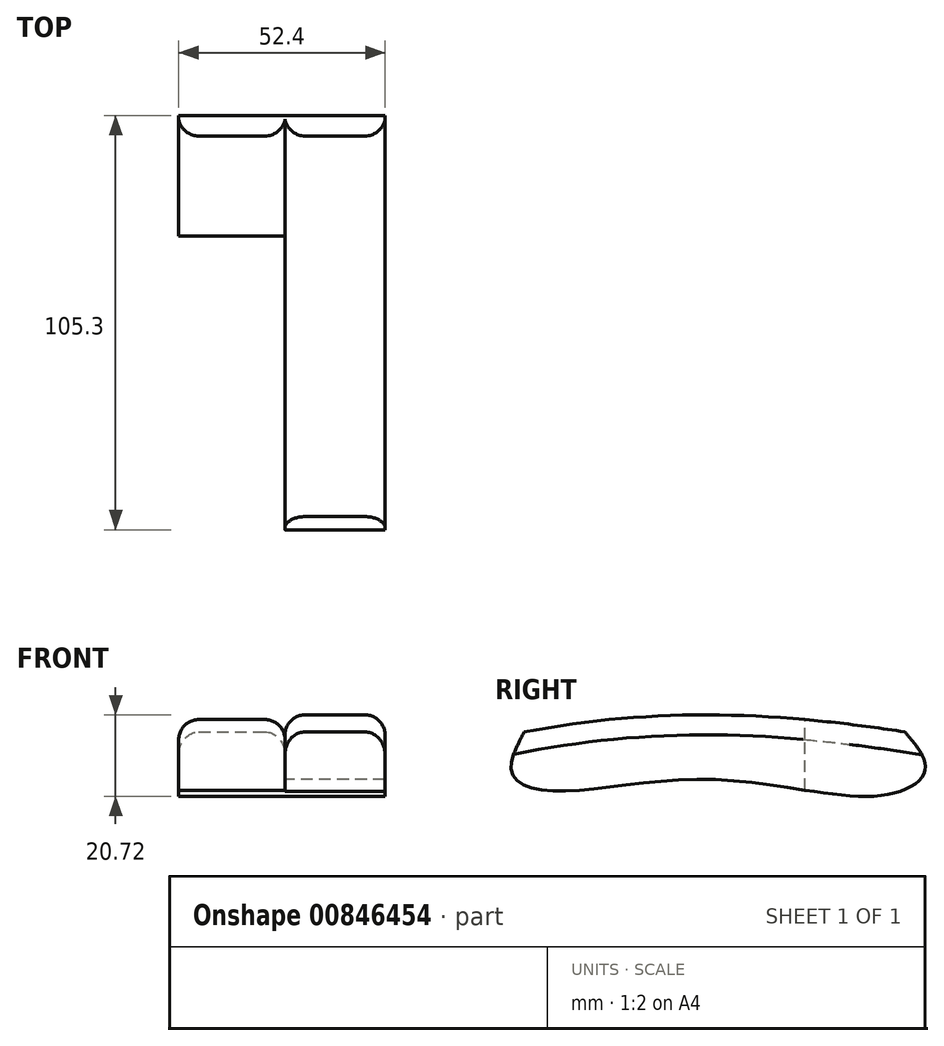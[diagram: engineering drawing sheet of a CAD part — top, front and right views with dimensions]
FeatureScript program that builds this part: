
annotation { "Feature Type Name" : "Feature", "Feature Type Description" : "" }
export const myFeature = defineFeature(function(context is Context, id is Id, definition is map)
    precondition{}
    {
        {
            var Q0;
            Q0=qCreatedBy(makeId("Right.planeOp"),FACE);
            var sketch = newSketch(context, id + "F0", { "sketchPlane" : qUnion([Q0])});
            skFitSpline(sketch, "E0", {"points": [v(49.07, 34.1) * mm, v(54.25, 24.6) * mm, v(43.6, 17.99) * mm, v(0, 22.02) * mm, v(-41.3, 19.14) * mm, v(-50.8, 23.74) * mm, v(-47.63, 34.1) * mm], "startDerivative": vector(67.95, -79.38) * mm, "endDerivative": vector(48.34, 92.2) * mm});
            skFitSpline(sketch, "E1", {"points": [v(-47.63, 34.1) * mm, v(49.07, 34.1) * mm], "startDerivative": vector(108.54, 20.43) * mm, "endDerivative": vector(91.54, -13.9) * mm});
            skLineSegment(sketch, "E2", {"start": v(23.69, 19.3) * mm, "end": v(23.69, 37.25) * mm});
            skSolve(sketch);
        }
        {
            var Q0;
            Q0=makeQuery(id+"F0.imprint","IMPRINT",FACE,{"disambiguationData":[TD([[makeQuery(id+"F0.imprint","IMPRINT",EDGE,{"derivedFrom":sQuery(id+"F0.wireOp",EDGE,"E0")}),-1.0]])]});
            extrude(context, id + "F1", {"entities" : qUnion([Q0]), "depth" : 25.4 * mm, "offsetDistance" : 25.4 * mm});
        }
        {
            var Q0;
            Q0=makeQuery(id+"F1.opExtrude","CAP_EDGE",EDGE,{"disambiguationData":[OSD([sQuery(id+"F0.wireOp",EDGE,"E1")])],"isStart":true});
            var Q1;
            Q1=makeQuery(id+"F1.opExtrude","CAP_EDGE",EDGE,{"disambiguationData":[OSD([sQuery(id+"F0.wireOp",EDGE,"E1")])],"isStart":false});
            fillet(context, id + "F2", {"entities" : qUnion([Q0, Q1]), "radius" : 5.08 * mm, "tangentPropagation" : true, "allowEdgeOverflow" : false});
        }
        {
            var Q0;
            {var subQ3=sQuery(id+"F0.wireOp",EDGE,"E2");Q0=makeQuery(id+"F0.imprint","IMPRINT",FACE,{"disambiguationData":[TD([[makeQuery(id+"F0.imprint","IMPRINT",EDGE,{"derivedFrom":subQ3}),-1.0]])]});}
            extrude(context, id + "F3", {"entities" : qUnion([Q0]), "operationType" : NewBodyOperationType.ADD, "oppositeDirection" : true, "depth" : 27 * mm, "offsetDistance" : 25.4 * mm});
        }
        {
            var Q0;
            Q0=makeQuery(id+"F3.opExtrude","CAP_EDGE",EDGE,{"disambiguationData":[OSD([sQuery(id+"F0.wireOp",EDGE,"E1")])],"isStart":false});
            var Q1;
            Q1=makeQuery(id+"F3.opExtrude","CAP_EDGE",EDGE,{"disambiguationData":[OSD([sQuery(id+"F0.wireOp",EDGE,"E1")])],"isStart":true});
            fillet(context, id + "F4", {"entities" : qUnion([Q0, Q1]), "radius" : 5.08 * mm, "tangentPropagation" : true, "allowEdgeOverflow" : false});
        }
    });
